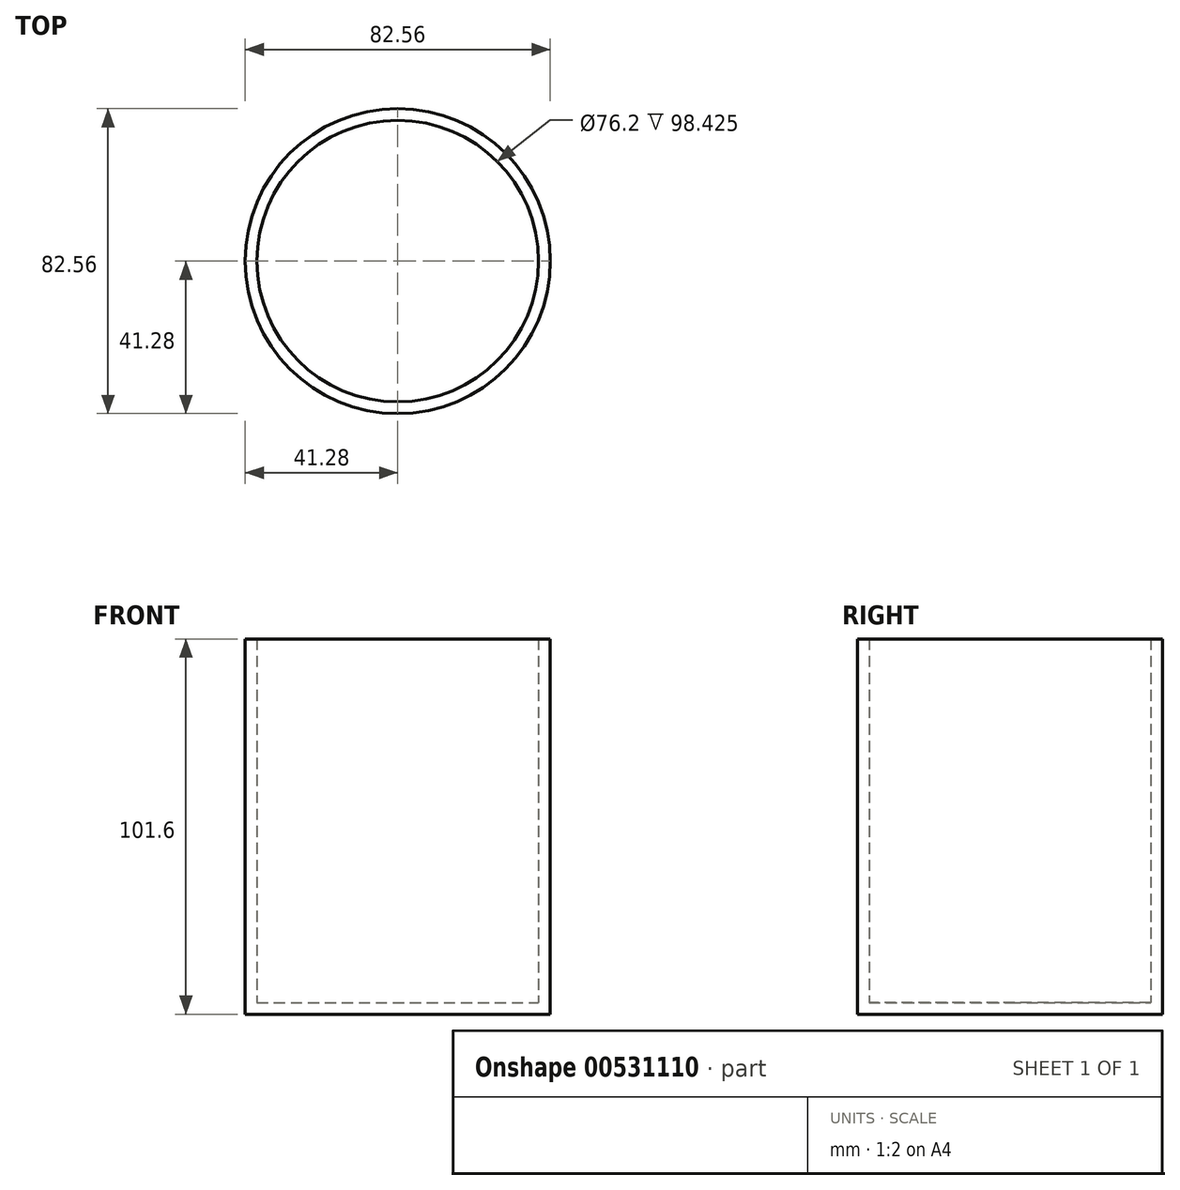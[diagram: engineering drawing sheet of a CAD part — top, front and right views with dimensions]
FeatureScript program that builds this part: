
annotation { "Feature Type Name" : "Feature", "Feature Type Description" : "" }
export const myFeature = defineFeature(function(context is Context, id is Id, definition is map)
    precondition{}
    {
        {
            var Q0;
            Q0=qCreatedBy(makeId("Front.planeOp"),FACE);
            var sketch = newSketch(context, id + "F0", { "sketchPlane" : qUnion([Q0])});
            skLineSegment(sketch, "E0.bottom", {"start": v(0, 0) * mm, "end": v(41.27, 0) * mm});
            skLineSegment(sketch, "E0.top", {"start": v(0, 3.18) * mm, "end": v(38.1, 3.18) * mm});
            skLineSegment(sketch, "E0.left", {"start": v(0, 0) * mm, "end": v(0, 3.18) * mm});
            skLineSegment(sketch, "E0.right", {"start": v(41.27, 0) * mm, "end": v(41.27, 3.18) * mm});
            skLineSegment(sketch, "E1.top", {"start": v(41.27, 101.6) * mm, "end": v(38.1, 101.6) * mm});
            skLineSegment(sketch, "E1.left", {"start": v(41.27, 3.17) * mm, "end": v(41.27, 101.6) * mm});
            skLineSegment(sketch, "E1.right", {"start": v(38.1, 3.17) * mm, "end": v(38.1, 101.6) * mm});
            skSolve(sketch);
        }
        {
            var Q0;
            Q0=makeQuery(id+"F0.imprint","IMPRINT",FACE,{"disambiguationData":[TD([[makeQuery(id+"F0.imprint","IMPRINT",EDGE,{"derivedFrom":sQuery(id+"F0.wireOp",EDGE,"E0.bottom")}),1.0]])]});
            var Q1;
            Q1=sQuery(id+"F0.wireOp",EDGE,"E0.left");
            revolve(context, id + "F1", {"entities" : qUnion([Q0]), "axis" : qUnion([Q1]), "revolveType" : RevolveType.FULL});
        }
    });
